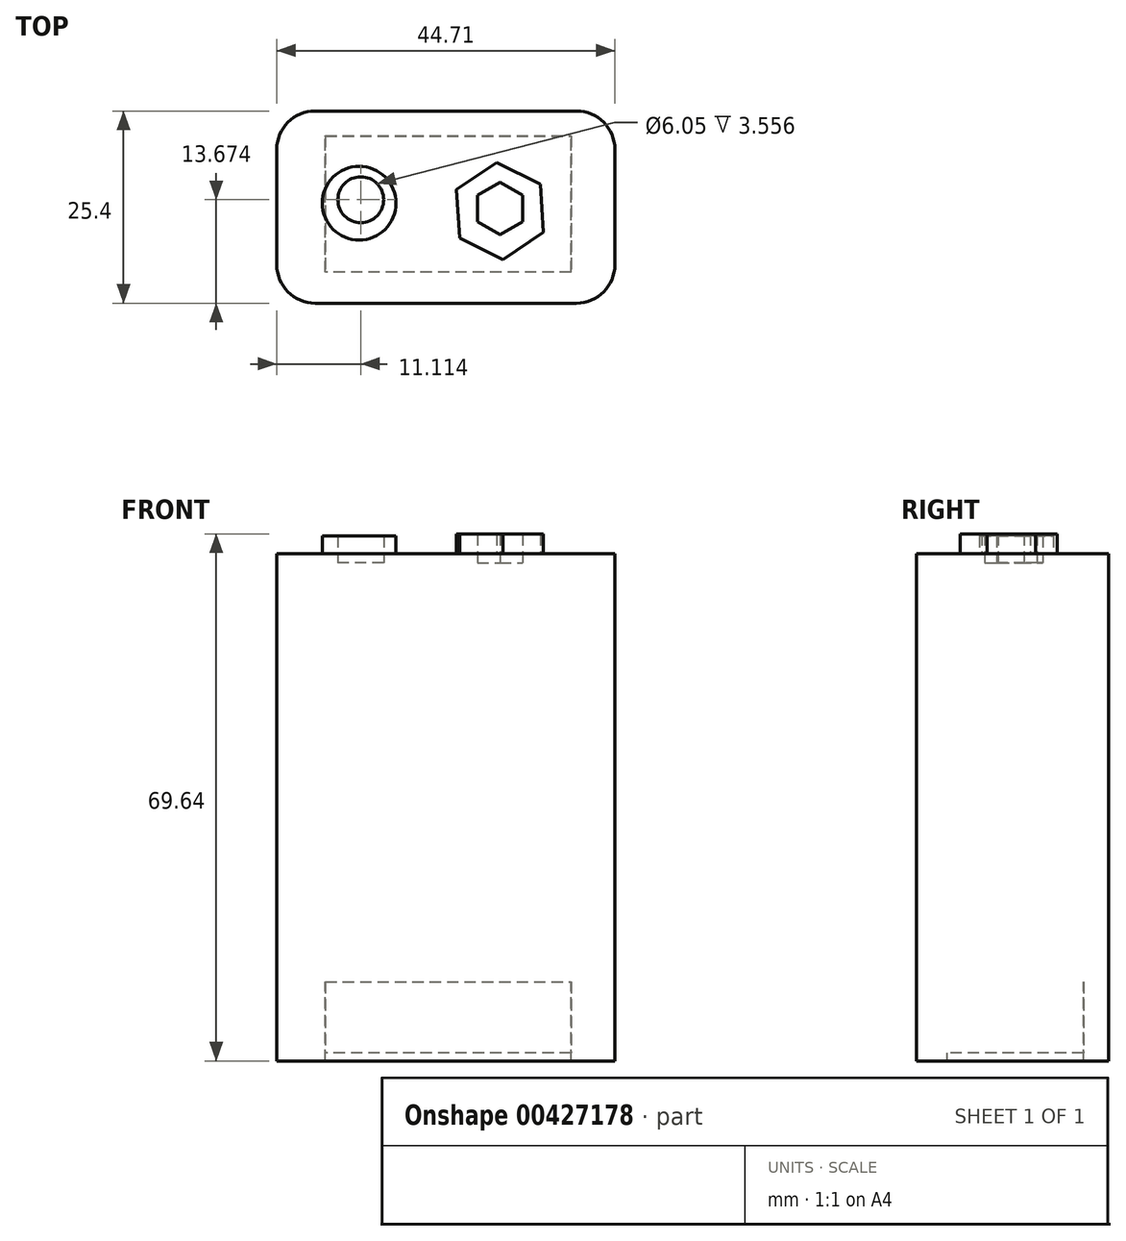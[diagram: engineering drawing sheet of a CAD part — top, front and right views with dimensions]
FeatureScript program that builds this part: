
annotation { "Feature Type Name" : "Feature", "Feature Type Description" : "" }
export const myFeature = defineFeature(function(context is Context, id is Id, definition is map)
    precondition{}
    {
        {
            var Q0;
            Q0=qCreatedBy(makeId("Front.planeOp"),FACE);
            var sketch = newSketch(context, id + "F0", { "sketchPlane" : qUnion([Q0])});
            skLineSegment(sketch, "E0.bottom", {"start": v(-29.52, 56.6) * mm, "end": v(15.19, 56.6) * mm});
            skLineSegment(sketch, "E0.top", {"start": v(-29.52, -10.46) * mm, "end": v(15.19, -10.46) * mm});
            skLineSegment(sketch, "E0.left", {"start": v(-29.52, 56.6) * mm, "end": v(-29.52, -10.46) * mm});
            skLineSegment(sketch, "E0.right", {"start": v(15.19, 56.6) * mm, "end": v(15.19, -10.46) * mm});
            skSolve(sketch);
        }
        {
            var Q0;
            Q0 = qSketchRegion(id + "F0", true);
            extrude(context, id + "F1", {"entities" : qUnion([Q0]), "depth" : 25.4 * mm});
        }
        {
            var Q0;
            Q0=makeQuery(id+"F1.opExtrude","CAP_EDGE",EDGE,{"disambiguationData":[OSD([sQuery(id+"F0.wireOp",EDGE,"E0.left")])],"isStart":false});
            var Q1;
            Q1=makeQuery(id+"F1.opExtrude","CAP_EDGE",EDGE,{"disambiguationData":[OSD([sQuery(id+"F0.wireOp",EDGE,"E0.right")])],"isStart":false});
            var Q2;
            Q2=makeQuery(id+"F1.opExtrude","CAP_EDGE",EDGE,{"disambiguationData":[OSD([sQuery(id+"F0.wireOp",EDGE,"E0.right")])],"isStart":true});
            var Q3;
            Q3=makeQuery(id+"F1.opExtrude","CAP_EDGE",EDGE,{"disambiguationData":[OSD([sQuery(id+"F0.wireOp",EDGE,"E0.left")])],"isStart":true});
            fillet(context, id + "F2", {"entities" : qUnion([Q0, Q1, Q2, Q3]), "radius" : 5.08 * mm, "tangentPropagation" : true, "allowEdgeOverflow" : false});
        }
        {
            var Q0;
            Q0=qCreatedBy(makeId("Top.planeOp"),FACE);
            var sketch = newSketch(context, id + "F3", { "sketchPlane" : qUnion([Q0])});
            skCircle(sketch, "E1", {"center": v(-18.63, -12.18) * mm, "radius": 4.87 * mm});
            skSolve(sketch);
        }
        {
            var Q0;
            Q0 = qSketchRegion(id + "F3", true);
            extrude(context, id + "F4", {"entities" : qUnion([Q0]), "operationType" : NewBodyOperationType.ADD, "depth" : 58.93 * mm});
        }
        {
            var Q0;
            Q0=qCreatedBy(makeId("Top.planeOp"),FACE);
            var sketch = newSketch(context, id + "F5", { "sketchPlane" : qUnion([Q0])});
            skCircle(sketch, "E2.cCircle", {"center": v(0, -13.21) * mm, "radius": 6.42 * mm, "construction": true});
            skLineSegment(sketch, "E2.0", {"start": v(-5.34, -16.77) * mm, "end": v(-5.76, -10.36) * mm});
            skLineSegment(sketch, "E2.1", {"start": v(-5.76, -10.36) * mm, "end": v(-0.41, -6.8) * mm});
            skLineSegment(sketch, "E2.2", {"start": v(-0.41, -6.8) * mm, "end": v(5.34, -9.65) * mm});
            skLineSegment(sketch, "E2.3", {"start": v(5.34, -9.65) * mm, "end": v(5.76, -16.06) * mm});
            skLineSegment(sketch, "E2.4", {"start": v(5.76, -16.06) * mm, "end": v(0.41, -19.62) * mm});
            skLineSegment(sketch, "E2.5", {"start": v(0.41, -19.62) * mm, "end": v(-5.34, -16.77) * mm});
            skSolve(sketch);
        }
        {
            var Q0;
            Q0 = qSketchRegion(id + "F5", true);
            extrude(context, id + "F6", {"entities" : qUnion([Q0]), "operationType" : NewBodyOperationType.ADD, "depth" : 59.18 * mm});
        }
        {
            var Q0;
            Q0=qCreatedBy(makeId("Top.planeOp"),FACE);
            var sketch = newSketch(context, id + "F7", { "sketchPlane" : qUnion([Q0])});
            skCircle(sketch, "E3", {"center": v(-18.4, -11.73) * mm, "radius": 3.03 * mm});
            skSolve(sketch);
        }
        {
            var Q0;
            Q0 = qSketchRegion(id + "F7", true);
            extrude(context, id + "F8", {"entities" : qUnion([Q0]), "operationType" : NewBodyOperationType.REMOVE, "depth" : 69.85 * mm});
        }
        {
            var Q0;
            Q0=qCreatedBy(makeId("Top.planeOp"),FACE);
            var sketch = newSketch(context, id + "F9", { "sketchPlane" : qUnion([Q0])});
            skCircle(sketch, "E4.cCircle", {"center": v(0, -12.87) * mm, "radius": 3.46 * mm, "construction": true});
            skLineSegment(sketch, "E4.0", {"start": v(0, -9.42) * mm, "end": v(3, -11.15) * mm});
            skLineSegment(sketch, "E4.1", {"start": v(3, -11.15) * mm, "end": v(3, -14.6) * mm});
            skLineSegment(sketch, "E4.2", {"start": v(3, -14.6) * mm, "end": v(0, -16.33) * mm});
            skLineSegment(sketch, "E4.3", {"start": v(0, -16.33) * mm, "end": v(-3, -14.6) * mm});
            skLineSegment(sketch, "E4.4", {"start": v(-3, -14.6) * mm, "end": v(-3, -11.15) * mm});
            skLineSegment(sketch, "E4.5", {"start": v(-3, -11.15) * mm, "end": v(0, -9.42) * mm});
            skSolve(sketch);
        }
        {
            var Q0;
            Q0 = qSketchRegion(id + "F9", true);
            extrude(context, id + "F10", {"entities" : qUnion([Q0]), "operationType" : NewBodyOperationType.REMOVE, "depth" : 63.25 * mm});
        }
        {
            var Q0;
            Q0=qCreatedBy(makeId("Top.planeOp"),FACE);
            var sketch = newSketch(context, id + "F11", { "sketchPlane" : qUnion([Q0])});
            skLineSegment(sketch, "E5.bottom", {"start": v(-22.56, -5.79) * mm, "end": v(10.1, -5.79) * mm});
            skLineSegment(sketch, "E5.top", {"start": v(-22.56, -21.23) * mm, "end": v(10.1, -21.23) * mm});
            skLineSegment(sketch, "E5.left", {"start": v(-22.56, -5.79) * mm, "end": v(-22.56, -21.23) * mm});
            skLineSegment(sketch, "E5.right", {"start": v(10.1, -5.79) * mm, "end": v(10.1, -21.23) * mm});
            skSolve(sketch);
        }
        {
            var Q0;
            Q0 = qSketchRegion(id + "F11", true);
            extrude(context, id + "F12", {"entities" : qUnion([Q0]), "operationType" : NewBodyOperationType.ADD, "depth" : 55.37 * mm});
        }
        {
            var Q0;
            Q0=qCreatedBy(makeId("Top.planeOp"),FACE);
            var sketch = newSketch(context, id + "F13", { "sketchPlane" : qUnion([Q0])});
            skLineSegment(sketch, "E6.bottom", {"start": v(-23.1, -21.32) * mm, "end": v(9.4, -21.32) * mm});
            skLineSegment(sketch, "E6.top", {"start": v(-23.1, -3.26) * mm, "end": v(9.4, -3.26) * mm});
            skLineSegment(sketch, "E6.left", {"start": v(-23.1, -21.32) * mm, "end": v(-23.1, -3.26) * mm});
            skLineSegment(sketch, "E6.right", {"start": v(9.4, -21.32) * mm, "end": v(9.4, -3.26) * mm});
            skSolve(sketch);
        }
        {
            var Q0;
            Q0 = qSketchRegion(id + "F13", true);
            extrude(context, id + "F14", {"entities" : qUnion([Q0]), "operationType" : NewBodyOperationType.REMOVE, "oppositeDirection" : true, "depth" : 12.2 * mm});
        }
        {
            var Q0;
            Q0=qCreatedBy(makeId("Top.planeOp"),FACE);
            var sketch = newSketch(context, id + "F15", { "sketchPlane" : qUnion([Q0])});
            skLineSegment(sketch, "E7.bottom", {"start": v(-24.92, -3.3) * mm, "end": v(11.68, -3.3) * mm});
            skLineSegment(sketch, "E7.top", {"start": v(-24.92, -21.77) * mm, "end": v(11.68, -21.77) * mm});
            skLineSegment(sketch, "E7.left", {"start": v(-24.92, -3.3) * mm, "end": v(-24.92, -21.77) * mm});
            skLineSegment(sketch, "E7.right", {"start": v(11.68, -3.3) * mm, "end": v(11.68, -21.77) * mm});
            skSolve(sketch);
        }
        {
            var Q0;
            Q0 = qSketchRegion(id + "F15", true);
            extrude(context, id + "F16", {"entities" : qUnion([Q0]), "operationType" : NewBodyOperationType.ADD, "oppositeDirection" : true, "depth" : 9.4 * mm});
        }
    });
